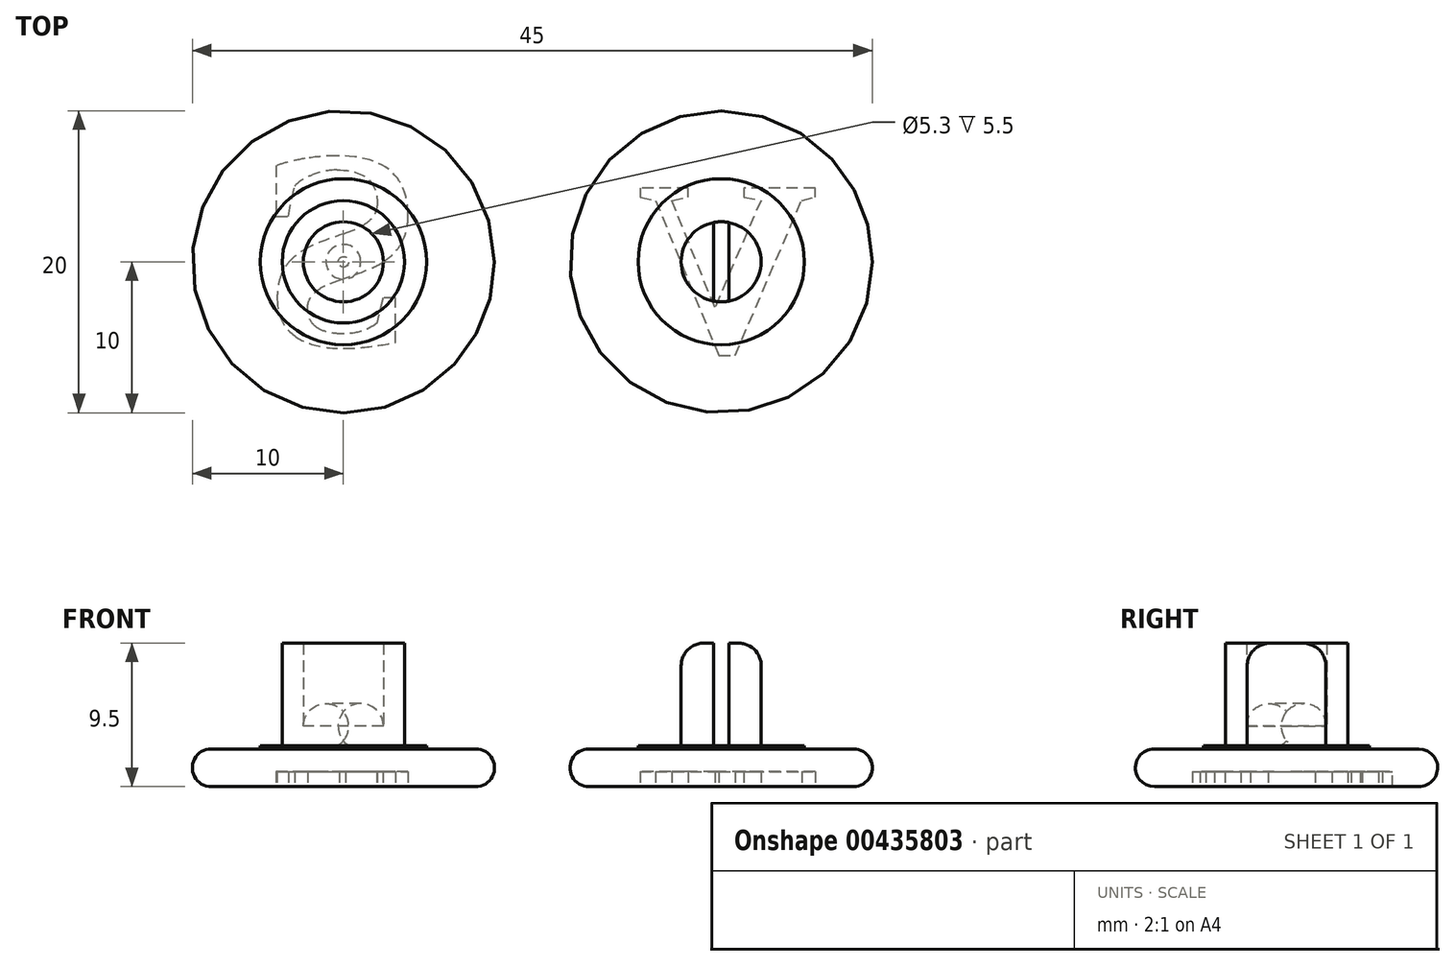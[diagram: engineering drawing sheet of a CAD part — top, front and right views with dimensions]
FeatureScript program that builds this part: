
annotation { "Feature Type Name" : "Feature", "Feature Type Description" : "" }
export const myFeature = defineFeature(function(context is Context, id is Id, definition is map)
    precondition{}
    {
        {
            var Q0;
            Q0=qCreatedBy(makeId("Top.planeOp"),FACE);
            var sketch = newSketch(context, id + "F0", { "sketchPlane" : qUnion([Q0])});
            skCircle(sketch, "E0", {"center": v(-25, 0) * mm, "radius": 10 * mm});
            skCircle(sketch, "E1", {"center": v(0, 0) * mm, "radius": 10 * mm});
            skSolve(sketch);
        }
        {
            var Q0;
            Q0=qSketchRegion(id+"F0",true);
            extrude(context, id + "F1", {"entities" : qUnion([Q0]), "depth" : 2.5 * mm, "offsetDistance" : 25 * mm});
        }
        {
            var Q0;
            Q0=makeQuery(id+"F1.opExtrude","CAP_FACE",FACE,{"disambiguationData":[OSD([sQuery(id+"F0.wireOp",EDGE,"E0")])],"isStart":false});
            var sketch = newSketch(context, id + "F2", { "sketchPlane" : qUnion([Q0])});
            skCircle(sketch, "E2", {"center": v(-25, 0) * mm, "radius": 4.05 * mm});
            skCircle(sketch, "E3", {"center": v(0, 0) * mm, "radius": 4.05 * mm});
            skCircle(sketch, "E4", {"center": v(-25, 0) * mm, "radius": 2.65 * mm});
            skCircle(sketch, "E5", {"center": v(0, 0) * mm, "radius": 2.65 * mm});
            skLineSegment(sketch, "E6", {"start": v(-0.5, 2.6) * mm, "end": v(-0.5, -2.6) * mm});
            skLineSegment(sketch, "E7", {"start": v(0.5, 2.6) * mm, "end": v(0.5, -2.6) * mm});
            skCircle(sketch, "E8", {"center": v(-25, 0) * mm, "radius": 5.5 * mm});
            skCircle(sketch, "E9", {"center": v(0, 0) * mm, "radius": 5.5 * mm});
            skSolve(sketch);
        }
        {
            var Q0;
            Q0=makeQuery(id+"F2.imprint","IMPRINT",FACE,{"disambiguationData":[TD([[makeQuery(id+"F2.imprint","IMPRINT",EDGE,{"derivedFrom":sQuery(id+"F2.wireOp",EDGE,"E2")}),1.0]])]});
            var Q1;
            {var subQ0=sQuery(id+"F2.wireOp",EDGE,"E7");Q1=makeQuery(id+"F2.imprint","IMPRINT",FACE,{"disambiguationData":[TD([[makeQuery(id+"F2.imprint","IMPRINT",EDGE,{"derivedFrom":subQ0}),1.0]])]});}
            var Q2;
            {var subQ0=sQuery(id+"F2.wireOp",EDGE,"E6");Q2=makeQuery(id+"F2.imprint","IMPRINT",FACE,{"disambiguationData":[TD([[makeQuery(id+"F2.imprint","IMPRINT",EDGE,{"derivedFrom":subQ0}),-1.0]])]});}
            extrude(context, id + "F3", {"entities" : qUnion([Q0, Q1, Q2]), "operationType" : NewBodyOperationType.ADD, "depth" : 7 * mm, "offsetDistance" : 25 * mm});
        }
        {
            var Q0;
            {var subQ0=sQuery(id+"F2.wireOp",EDGE,"E7");var subQ1=sQuery(id+"F2.wireOp",EDGE,"E5");Q0=makeQuery(id+"F3.opExtrude","CAP_EDGE",EDGE,{"disambiguationData":[OSD([subQ1]),TDD([makeQuery(id+"F2.imprint","IMPRINT",EDGE,{"disambiguationData":[TD([[makeQuery(id+"F2.imprint","INTERSECT",VERTEX,{"disambiguationData":[OD(0.0)],"derivedFrom":[subQ1,subQ0]}),1.0]])],"derivedFrom":subQ1})])],"isStart":false});}
            var Q1;
            {var subQ0=sQuery(id+"F2.wireOp",EDGE,"E6");var subQ1=sQuery(id+"F2.wireOp",EDGE,"E5");Q1=makeQuery(id+"F3.opExtrude","CAP_EDGE",EDGE,{"disambiguationData":[OSD([subQ1]),TDD([makeQuery(id+"F2.imprint","IMPRINT",EDGE,{"disambiguationData":[TD([[makeQuery(id+"F2.imprint","INTERSECT",VERTEX,{"disambiguationData":[OD(0.0)],"derivedFrom":[subQ1,subQ0]}),-1.0]])],"derivedFrom":subQ1})])],"isStart":false});}
            fillet(context, id + "F4", {"entities" : qUnion([Q0, Q1]), "radius" : 1.5 * mm, "tangentPropagation" : true, "allowEdgeOverflow" : false});
        }
        {
            var Q0;
            Q0=makeQuery(id+"F3.opExtrude","CAP_EDGE",EDGE,{"disambiguationData":[OSD([sQuery(id+"F2.wireOp",EDGE,"E4")])],"isStart":true});
            fillet(context, id + "F5", {"entities" : qUnion([Q0]), "radius" : 1.5 * mm, "tangentPropagation" : true, "allowEdgeOverflow" : false});
        }
        {
            var Q0;
            Q0=makeQuery(id+"F1.opExtrude","CAP_EDGE",EDGE,{"disambiguationData":[OSD([sQuery(id+"F0.wireOp",EDGE,"E0")])],"isStart":false});
            var Q1;
            Q1=makeQuery(id+"F1.opExtrude","CAP_EDGE",EDGE,{"disambiguationData":[OSD([sQuery(id+"F0.wireOp",EDGE,"E1")])],"isStart":true});
            var Q2;
            Q2=makeQuery(id+"F1.opExtrude","CAP_EDGE",EDGE,{"disambiguationData":[OSD([sQuery(id+"F0.wireOp",EDGE,"E0")])],"isStart":true});
            var Q3;
            Q3=makeQuery(id+"F1.opExtrude","CAP_EDGE",EDGE,{"disambiguationData":[OSD([sQuery(id+"F0.wireOp",EDGE,"E1")])],"isStart":false});
            fillet(context, id + "F6", {"entities" : qUnion([Q0, Q1, Q2, Q3]), "radius" : 1.25 * mm, "tangentPropagation" : true, "allowEdgeOverflow" : false});
        }
        {
            var Q0;
            Q0=makeQuery(id+"F1.opExtrude","CAP_FACE",FACE,{"disambiguationData":[OSD([sQuery(id+"F0.wireOp",EDGE,"E1")])],"isStart":true});
            var sketch = newSketch(context, id + "F7", { "sketchPlane" : qUnion([Q0])});
            skText(sketch, "E10", { "text": "V", "fontName": "Tinos-Bold.ttf"});
            skText(sketch, "E11", { "text": "S", "fontName": "Tinos-Bold.ttf"});
            const initialGuessF7  = {"E10": [0.0064, 0.00596, -1, 0, 0.01192], "E11": [-0.03047, -0.00683, 1, 0, 0.01366]};
            skSetInitialGuess(sketch, initialGuessF7);
            skSolve(sketch);
        }
        {
            var Q0;
            Q0 = qSketchRegion(id + "F7", true);
            extrude(context, id + "F8", {"entities" : qUnion([Q0]), "operationType" : NewBodyOperationType.REMOVE, "oppositeDirection" : true, "depth" : 1 * mm, "offsetDistance" : 25 * mm});
        }
        {
            var Q0;
            Q0=makeQuery(id+"F2.imprint","IMPRINT",FACE,{"disambiguationData":[TD([[makeQuery(id+"F2.imprint","IMPRINT",EDGE,{"derivedFrom":sQuery(id+"F2.wireOp",EDGE,"E2")}),-1.0]])]});
            var Q1;
            Q1=makeQuery(id+"F2.imprint","IMPRINT",FACE,{"disambiguationData":[TD([[makeQuery(id+"F2.imprint","IMPRINT",EDGE,{"derivedFrom":sQuery(id+"F2.wireOp",EDGE,"E3")}),-1.0]])]});
            var Q2;
            Q2=makeQuery(id+"F2.imprint","IMPRINT",FACE,{"disambiguationData":[TD([[makeQuery(id+"F2.imprint","IMPRINT",EDGE,{"derivedFrom":sQuery(id+"F2.wireOp",EDGE,"E3")}),1.0]])]});
            extrude(context, id + "F9", {"entities" : qUnion([Q0, Q1, Q2]), "operationType" : NewBodyOperationType.ADD, "depth" : .2 * mm, "offsetDistance" : 25 * mm});
        }
    });
